# Revit family: Ленточный арочный зенитный фонарь M8CITY_А_ВЕНТ-ДЫМ_1_ств
name_source: partatom
category: Оборудование
revit_build: Autodesk Revit 2017 (Build: 20170118_1100(x64)
units: mm (PartAtom-declared; Revit-internal decimal feet)

## family parameters
Всегда вертикально = Нет
Общий = Нет
Основа = Крыша
При загрузке вырезать с полостями = Нет
Размер круглого соединителя = Использовать диаметр
Тип детали = Нормальный
Точка расчета площади = Нет

## types (1)
- Зенитный фонарь M8CITY Л-А-1 створка
    URL = www.m8city.by
    Высота = 800 мм
    Высота основания = 727 мм
    Длина = 6000 мм
    Длина ПК = 2515 мм
    Длина проёма = 6000 мм
    Длина проёма ввод = 6000 мм
    Длина створки = 1500 мм
    Изготовитель = ООО Завод М8 Сити Про
    Количество арок = 3
    Описание = Ленточный зенитный фонарь M8CITY в премиальном исполнении со створкой дымоудаления/вентиляции с арочным сводом
    Типовой растр = 1060 мм
    Шаг типовой = 1060 мм
    Ширина = 3380 мм
    Ширина проёма = 3380 мм
    Ширина проёма ввод = 3380 мм
